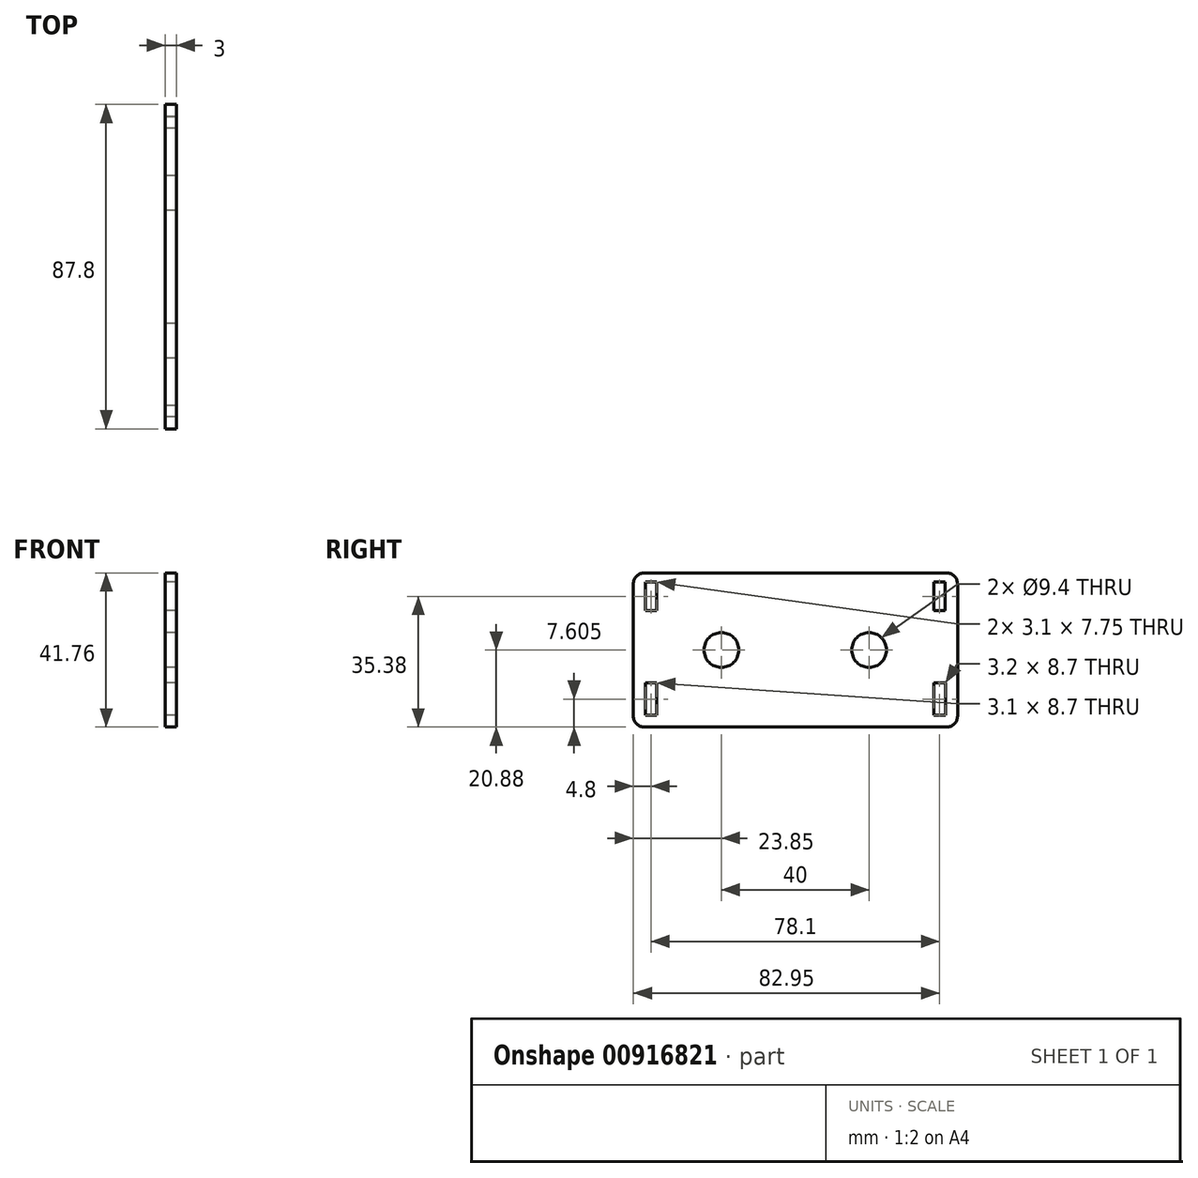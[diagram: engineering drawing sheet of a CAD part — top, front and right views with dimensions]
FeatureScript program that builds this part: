
annotation { "Feature Type Name" : "Feature", "Feature Type Description" : "" }
export const myFeature = defineFeature(function(context is Context, id is Id, definition is map)
    precondition{}
    {
        {
            var Q0;
            Q0=qCreatedBy(makeId("Right.planeOp"),FACE);
            var sketch = newSketch(context, id + "F0", { "sketchPlane" : qUnion([Q0])});
            skLineSegment(sketch, "E0.bottom", {"start": v(-43.85, 20.88) * mm, "end": v(43.95, 20.88) * mm});
            skLineSegment(sketch, "E0.top", {"start": v(-43.85, -20.88) * mm, "end": v(43.95, -20.88) * mm});
            skLineSegment(sketch, "E0.left", {"start": v(-43.85, 20.88) * mm, "end": v(-43.85, -20.88) * mm});
            skLineSegment(sketch, "E0.right", {"start": v(43.95, 20.88) * mm, "end": v(43.95, -20.88) * mm});
            skLineSegment(sketch, "E1.bottom", {"start": v(-40.6, 18.38) * mm, "end": v(-37.5, 18.38) * mm});
            skLineSegment(sketch, "E1.top", {"start": v(-40.6, 10.62) * mm, "end": v(-37.5, 10.62) * mm});
            skLineSegment(sketch, "E1.left", {"start": v(-40.6, 18.38) * mm, "end": v(-40.6, 10.62) * mm});
            skLineSegment(sketch, "E1.right", {"start": v(-37.5, 18.38) * mm, "end": v(-37.5, 10.62) * mm});
            skLineSegment(sketch, "E2.bottom", {"start": v(-40.6, -8.93) * mm, "end": v(-37.5, -8.93) * mm});
            skLineSegment(sketch, "E2.top", {"start": v(-40.6, -17.62) * mm, "end": v(-37.5, -17.62) * mm});
            skLineSegment(sketch, "E2.left", {"start": v(-40.6, -8.93) * mm, "end": v(-40.6, -17.62) * mm});
            skLineSegment(sketch, "E2.right", {"start": v(-37.5, -8.93) * mm, "end": v(-37.5, -17.62) * mm});
            skLineSegment(sketch, "E3.MirrorCS", {"start": v(40.7, -8.92) * mm, "end": v(37.5, -8.92) * mm});
            skLineSegment(sketch, "E4.MirrorCS", {"start": v(40.7, -8.92) * mm, "end": v(40.7, -17.62) * mm});
            skLineSegment(sketch, "E5.MirrorCS", {"start": v(40.7, -17.62) * mm, "end": v(37.5, -17.62) * mm});
            skLineSegment(sketch, "E6.MirrorCS", {"start": v(37.5, -8.92) * mm, "end": v(37.5, -17.62) * mm});
            skCircle(sketch, "E7", {"center": v(-20, 0) * mm, "radius": 4.7 * mm});
            skCircle(sketch, "E8.MirrorC", {"center": v(20, 0) * mm, "radius": 4.7 * mm});
            skLineSegment(sketch, "E9.MirrorCS", {"start": v(40.6, 18.38) * mm, "end": v(37.5, 18.38) * mm});
            skLineSegment(sketch, "E10.MirrorCS", {"start": v(37.5, 18.38) * mm, "end": v(37.5, 10.62) * mm});
            skLineSegment(sketch, "E11.MirrorCS", {"start": v(40.6, 18.38) * mm, "end": v(40.6, 10.62) * mm});
            skLineSegment(sketch, "E12.MirrorCS", {"start": v(40.6, 10.62) * mm, "end": v(37.5, 10.62) * mm});
            skSolve(sketch);
        }
        {
            var Q0;
            Q0=qSketchRegion(id+"F0",true);
            extrude(context, id + "F1", {"entities" : qUnion([Q0]), "depth" : 3 * mm, "offsetDistance" : 25 * mm});
        }
        {
            var Q0;
            Q0=makeQuery(id+"F1.opExtrude","SWEPT_EDGE",EDGE,{"disambiguationData":[OSD([sQuery(id+"F0.wireOp",EDGE,"E0.bottom"),sQuery(id+"F0.wireOp",EDGE,"E0.left")])]});
            var Q1;
            Q1=makeQuery(id+"F1.opExtrude","SWEPT_EDGE",EDGE,{"disambiguationData":[OSD([sQuery(id+"F0.wireOp",EDGE,"E0.top"),sQuery(id+"F0.wireOp",EDGE,"E0.left")])]});
            var Q2;
            Q2=makeQuery(id+"F1.opExtrude","SWEPT_EDGE",EDGE,{"disambiguationData":[OSD([sQuery(id+"F0.wireOp",EDGE,"E0.bottom"),sQuery(id+"F0.wireOp",EDGE,"E0.right")])]});
            var Q3;
            Q3=makeQuery(id+"F1.opExtrude","SWEPT_EDGE",EDGE,{"disambiguationData":[OSD([sQuery(id+"F0.wireOp",EDGE,"E0.top"),sQuery(id+"F0.wireOp",EDGE,"E0.right")])]});
            fillet(context, id + "F2", {"entities" : qUnion([Q0, Q1, Q2, Q3]), "radius" : 3 * mm, "tangentPropagation" : true, "allowEdgeOverflow" : false});
        }
    });
